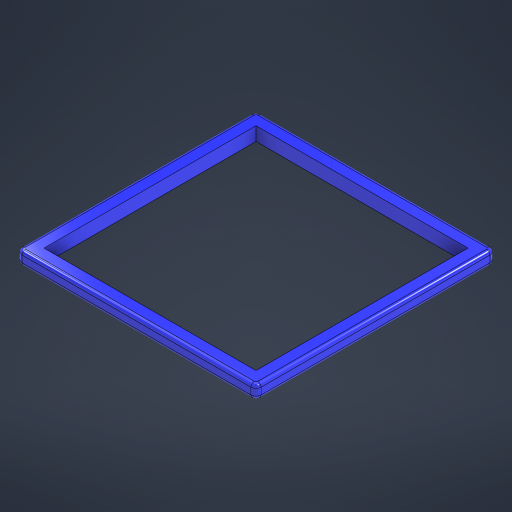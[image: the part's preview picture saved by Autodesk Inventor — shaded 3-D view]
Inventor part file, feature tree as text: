
AUTODESK INVENTOR PART (.ipt)
format: ipt  version: 2023.1 (Build 271208000, 208)  size: 233,984 bytes
history: native  units: in
note: dims shown in document units (in); Inventor stores cm internally (conversion verified against a paired STEP export)
features: fillet x2, extrude x1, sketch x1
ambient origin geometry x8: Origin, YZ Plane, XZ Plane, XY Plane, X Axis, Y Axis, Z Axis, Center Point
bodies: Solid1 (feature_tree)
feature tree (4):
  extrude  "Extrusion1"  Depth=2.0in
  fillet  "Fillet1"  Radius=2.0in
  fillet  "Fillet2"  Radius=2.0in
  sketch  "Sketch1"  dims[d0=31.25in d1=2.0in d2=2.0in d3=2.0in d4=0.0in d5=0.5in d6=0.75in]
